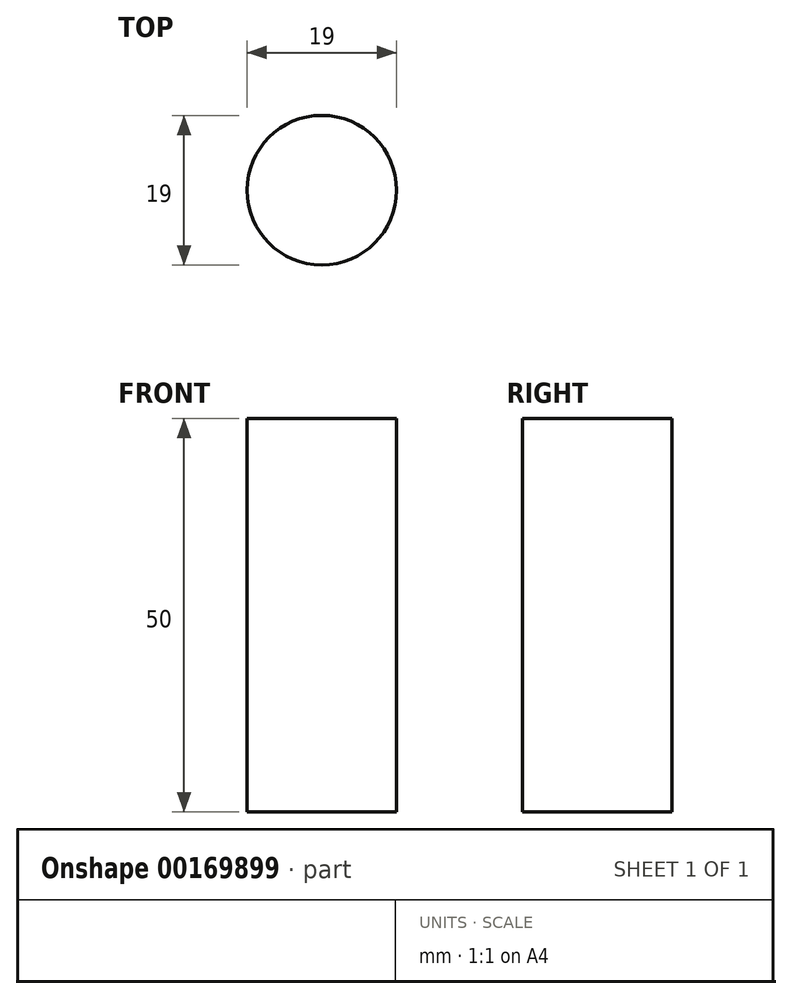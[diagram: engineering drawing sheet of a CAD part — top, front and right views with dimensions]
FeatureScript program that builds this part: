
annotation { "Feature Type Name" : "Feature", "Feature Type Description" : "" }
export const myFeature = defineFeature(function(context is Context, id is Id, definition is map)
    precondition{}
    {
        {
            var Q0;
            Q0=qCreatedBy(makeId("Top.planeOp"),FACE);
            var sketch = newSketch(context, id + "F0", { "sketchPlane" : qUnion([Q0])});
            skCircle(sketch, "E0", {"center": v(0, 0) * mm, "radius": 9.5 * mm});
            skSolve(sketch);
        }
        {
            var Q0;
            Q0 = qSketchRegion(id + "F0", true);
            extrude(context, id + "F1", {"entities" : qUnion([Q0]), "depth" : 50 * mm});
        }
    });
